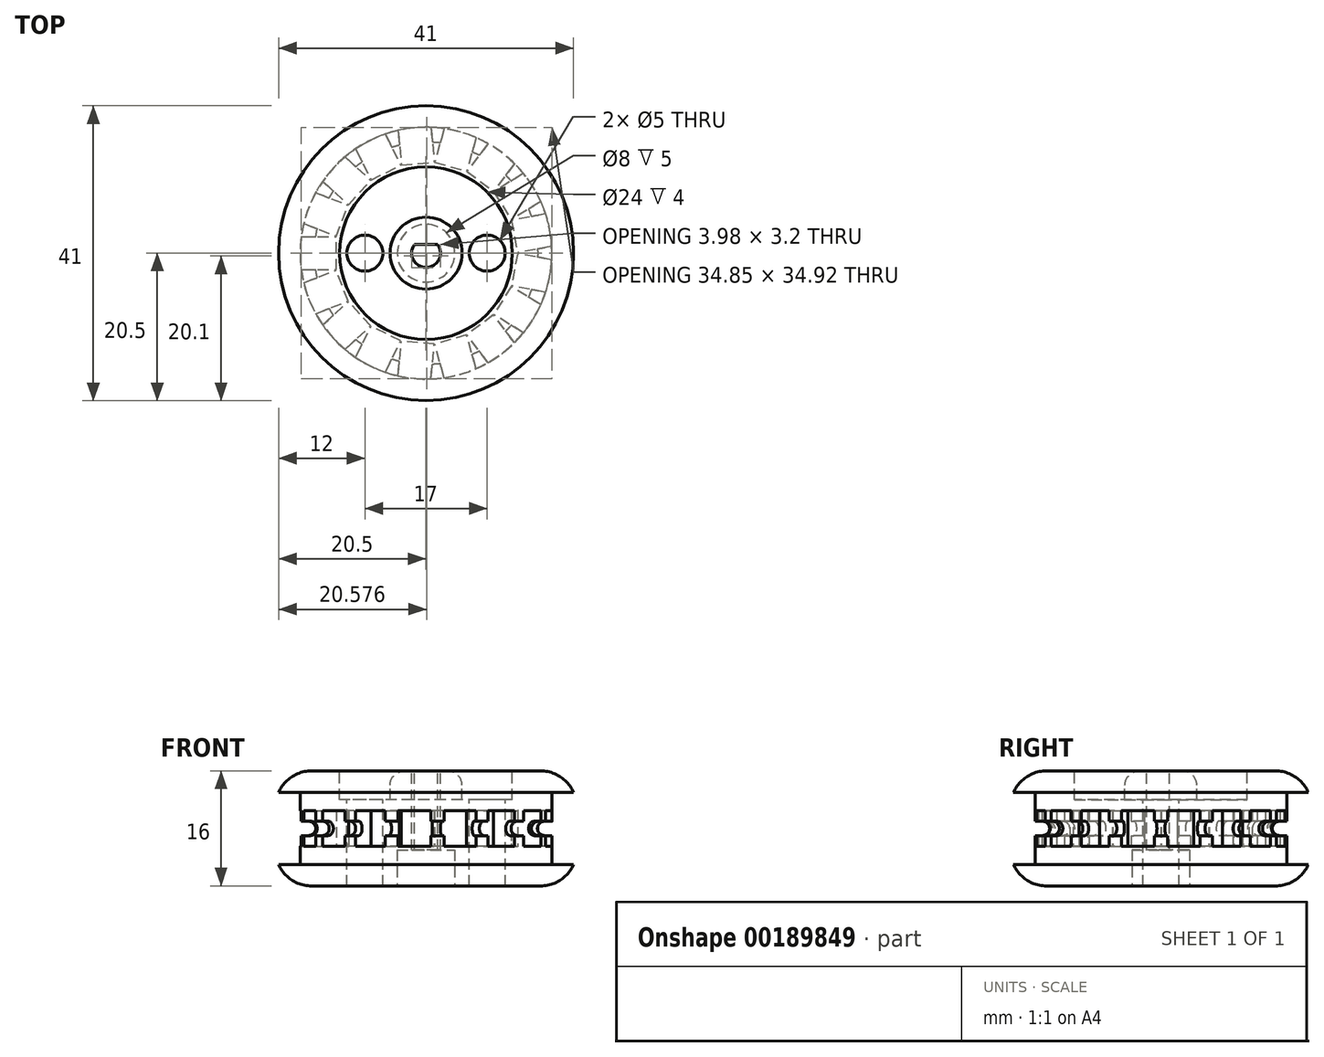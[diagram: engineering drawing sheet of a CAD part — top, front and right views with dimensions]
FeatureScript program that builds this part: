
annotation { "Feature Type Name" : "Feature", "Feature Type Description" : "" }
export const myFeature = defineFeature(function(context is Context, id is Id, definition is map)
    precondition{}
    {
        {
            var Q0;
            Q0=qCreatedBy(makeId("Top.planeOp"),FACE);
            var sketch = newSketch(context, id + "F0", { "sketchPlane" : qUnion([Q0])});
            skCircle(sketch, "E0", {"center": v(0, 0) * mm, "radius": 17.5 * mm});
            skSolve(sketch);
        }
        {
            var Q0;
            Q0=makeQuery(id+"F0.imprint","IMPRINT",FACE,{"disambiguationData":[TD([[makeQuery(id+"F0.imprint","IMPRINT",EDGE,{"derivedFrom":sQuery(id+"F0.wireOp",EDGE,"E0")}),1.0]])]});
            extrude(context, id + "F1", {"entities" : qUnion([Q0]), "depth" : 10 * mm});
        }
        {
            var Q0;
            Q0=makeQuery(id+"F1.opExtrude","CAP_FACE",FACE,{"disambiguationData":[OSD([sQuery(id+"F0.wireOp",EDGE,"E0")])],"isStart":false});
            cPlane(context, id + "F2", {"entities" : qUnion([Q0]), "cplaneType" : CPlaneType.OFFSET, "offset" : 5 * mm, "oppositeDirection" : true, "width" : 150 * mm, "height" : 150 * mm});
        }
        {
            var Q0;
            Q0=qCreatedBy(id+"F2.planeOp",FACE);
            var sketch = newSketch(context, id + "F3", { "sketchPlane" : qUnion([Q0])});
            skLineSegment(sketch, "E1.bottom", {"start": v(-17.5, -2.3) * mm, "end": v(-12.5, -2.3) * mm});
            skLineSegment(sketch, "E1.top", {"start": v(-17.5, 2.3) * mm, "end": v(-12.5, 2.3) * mm});
            skLineSegment(sketch, "E1.left", {"start": v(-17.5, -2.3) * mm, "end": v(-17.5, 2.3) * mm});
            skLineSegment(sketch, "E1.right", {"start": v(-12.5, -2.3) * mm, "end": v(-12.5, 2.3) * mm});
            skPoint(sketch, "E2", {"position": v(-12.5, 0) * mm});
            skLineSegment(sketch, "E3.1.0", {"start": v(-15.49, -8.47) * mm, "end": v(-10.83, -6.66) * mm});
            skLineSegment(sketch, "E3.1.1", {"start": v(-15.49, -8.47) * mm, "end": v(-17.15, -4.18) * mm});
            skLineSegment(sketch, "E3.1.2", {"start": v(-10.83, -6.66) * mm, "end": v(-12.49, -2.37) * mm});
            skLineSegment(sketch, "E3.1.3", {"start": v(-17.15, -4.18) * mm, "end": v(-12.49, -2.37) * mm});
            skLineSegment(sketch, "E3.2.0", {"start": v(-11.38, -13.49) * mm, "end": v(-7.69, -10.12) * mm});
            skLineSegment(sketch, "E3.2.1", {"start": v(-11.38, -13.49) * mm, "end": v(-14.48, -10.09) * mm});
            skLineSegment(sketch, "E3.2.2", {"start": v(-7.69, -10.12) * mm, "end": v(-10.79, -6.72) * mm});
            skLineSegment(sketch, "E3.2.3", {"start": v(-14.48, -10.09) * mm, "end": v(-10.79, -6.72) * mm});
            skLineSegment(sketch, "E3.3.0", {"start": v(-5.74, -16.7) * mm, "end": v(-3.51, -12.21) * mm});
            skLineSegment(sketch, "E3.3.1", {"start": v(-5.74, -16.7) * mm, "end": v(-9.86, -14.64) * mm});
            skLineSegment(sketch, "E3.3.2", {"start": v(-3.51, -12.21) * mm, "end": v(-7.63, -10.16) * mm});
            skLineSegment(sketch, "E3.3.3", {"start": v(-9.86, -14.64) * mm, "end": v(-7.63, -10.16) * mm});
            skLineSegment(sketch, "E3.4.0", {"start": v(0.68, -17.64) * mm, "end": v(1.14, -12.66) * mm});
            skLineSegment(sketch, "E3.4.1", {"start": v(0.68, -17.64) * mm, "end": v(-3.9, -17.21) * mm});
            skLineSegment(sketch, "E3.4.2", {"start": v(1.14, -12.66) * mm, "end": v(-3.44, -12.23) * mm});
            skLineSegment(sketch, "E3.4.3", {"start": v(-3.9, -17.21) * mm, "end": v(-3.44, -12.23) * mm});
            skLineSegment(sketch, "E3.5.0", {"start": v(7, -16.2) * mm, "end": v(5.63, -11.4) * mm});
            skLineSegment(sketch, "E3.5.1", {"start": v(7, -16.2) * mm, "end": v(2.58, -17.46) * mm});
            skLineSegment(sketch, "E3.5.2", {"start": v(5.63, -11.4) * mm, "end": v(1.2, -12.65) * mm});
            skLineSegment(sketch, "E3.5.3", {"start": v(2.58, -17.46) * mm, "end": v(1.2, -12.65) * mm});
            skLineSegment(sketch, "E3.6.0", {"start": v(12.38, -12.58) * mm, "end": v(9.37, -8.59) * mm});
            skLineSegment(sketch, "E3.6.1", {"start": v(12.38, -12.58) * mm, "end": v(8.71, -15.35) * mm});
            skLineSegment(sketch, "E3.6.2", {"start": v(9.37, -8.59) * mm, "end": v(5.7, -11.36) * mm});
            skLineSegment(sketch, "E3.6.3", {"start": v(8.71, -15.35) * mm, "end": v(5.7, -11.36) * mm});
            skLineSegment(sketch, "E3.7.0", {"start": v(16.09, -7.26) * mm, "end": v(11.84, -4.62) * mm});
            skLineSegment(sketch, "E3.7.1", {"start": v(16.09, -7.26) * mm, "end": v(13.67, -11.17) * mm});
            skLineSegment(sketch, "E3.7.2", {"start": v(11.84, -4.62) * mm, "end": v(9.42, -8.54) * mm});
            skLineSegment(sketch, "E3.7.3", {"start": v(13.67, -11.17) * mm, "end": v(9.42, -8.54) * mm});
            skLineSegment(sketch, "E3.8.0", {"start": v(17.62, -0.95) * mm, "end": v(12.7, -0.04) * mm});
            skLineSegment(sketch, "E3.8.1", {"start": v(17.62, -0.95) * mm, "end": v(16.78, -5.48) * mm});
            skLineSegment(sketch, "E3.8.2", {"start": v(12.7, -0.04) * mm, "end": v(11.86, -4.56) * mm});
            skLineSegment(sketch, "E3.8.3", {"start": v(16.78, -5.48) * mm, "end": v(11.86, -4.56) * mm});
            skLineSegment(sketch, "E3.9.0", {"start": v(16.78, 5.48) * mm, "end": v(11.86, 4.56) * mm});
            skLineSegment(sketch, "E3.9.1", {"start": v(16.78, 5.48) * mm, "end": v(17.62, 0.95) * mm});
            skLineSegment(sketch, "E3.9.2", {"start": v(11.86, 4.56) * mm, "end": v(12.7, 0.04) * mm});
            skLineSegment(sketch, "E3.9.3", {"start": v(17.62, 0.95) * mm, "end": v(12.7, 0.04) * mm});
            skLineSegment(sketch, "E3.10.0", {"start": v(13.67, 11.17) * mm, "end": v(9.42, 8.54) * mm});
            skLineSegment(sketch, "E3.10.1", {"start": v(13.67, 11.17) * mm, "end": v(16.09, 7.26) * mm});
            skLineSegment(sketch, "E3.10.2", {"start": v(9.42, 8.54) * mm, "end": v(11.84, 4.62) * mm});
            skLineSegment(sketch, "E3.10.3", {"start": v(16.09, 7.26) * mm, "end": v(11.84, 4.62) * mm});
            skLineSegment(sketch, "E3.11.0", {"start": v(8.71, 15.35) * mm, "end": v(5.7, 11.36) * mm});
            skLineSegment(sketch, "E3.11.1", {"start": v(8.71, 15.35) * mm, "end": v(12.38, 12.58) * mm});
            skLineSegment(sketch, "E3.11.2", {"start": v(5.7, 11.36) * mm, "end": v(9.37, 8.59) * mm});
            skLineSegment(sketch, "E3.11.3", {"start": v(12.38, 12.58) * mm, "end": v(9.37, 8.59) * mm});
            skLineSegment(sketch, "E3.12.0", {"start": v(2.58, 17.46) * mm, "end": v(1.2, 12.65) * mm});
            skLineSegment(sketch, "E3.12.1", {"start": v(2.58, 17.46) * mm, "end": v(7, 16.2) * mm});
            skLineSegment(sketch, "E3.12.2", {"start": v(1.2, 12.65) * mm, "end": v(5.63, 11.4) * mm});
            skLineSegment(sketch, "E3.12.3", {"start": v(7, 16.2) * mm, "end": v(5.63, 11.4) * mm});
            skLineSegment(sketch, "E3.13.0", {"start": v(-3.9, 17.21) * mm, "end": v(-3.44, 12.23) * mm});
            skLineSegment(sketch, "E3.13.1", {"start": v(-3.9, 17.21) * mm, "end": v(0.68, 17.64) * mm});
            skLineSegment(sketch, "E3.13.2", {"start": v(-3.44, 12.23) * mm, "end": v(1.14, 12.66) * mm});
            skLineSegment(sketch, "E3.13.3", {"start": v(0.68, 17.64) * mm, "end": v(1.14, 12.66) * mm});
            skLineSegment(sketch, "E3.14.0", {"start": v(-9.86, 14.64) * mm, "end": v(-7.63, 10.16) * mm});
            skLineSegment(sketch, "E3.14.1", {"start": v(-9.86, 14.64) * mm, "end": v(-5.74, 16.7) * mm});
            skLineSegment(sketch, "E3.14.2", {"start": v(-7.63, 10.16) * mm, "end": v(-3.51, 12.21) * mm});
            skLineSegment(sketch, "E3.14.3", {"start": v(-5.74, 16.7) * mm, "end": v(-3.51, 12.21) * mm});
            skLineSegment(sketch, "E3.15.0", {"start": v(-14.48, 10.09) * mm, "end": v(-10.79, 6.72) * mm});
            skLineSegment(sketch, "E3.15.1", {"start": v(-14.48, 10.09) * mm, "end": v(-11.38, 13.49) * mm});
            skLineSegment(sketch, "E3.15.2", {"start": v(-10.79, 6.72) * mm, "end": v(-7.69, 10.12) * mm});
            skLineSegment(sketch, "E3.15.3", {"start": v(-11.38, 13.49) * mm, "end": v(-7.69, 10.12) * mm});
            skLineSegment(sketch, "E3.16.0", {"start": v(-17.15, 4.18) * mm, "end": v(-12.49, 2.37) * mm});
            skLineSegment(sketch, "E3.16.1", {"start": v(-17.15, 4.18) * mm, "end": v(-15.49, 8.47) * mm});
            skLineSegment(sketch, "E3.16.2", {"start": v(-12.49, 2.37) * mm, "end": v(-10.83, 6.66) * mm});
            skLineSegment(sketch, "E3.16.3", {"start": v(-15.49, 8.47) * mm, "end": v(-10.83, 6.66) * mm});
            skPoint(sketch, "E3.center", {"position": v(0, 0) * mm});
            skSolve(sketch);
        }
        {
            var Q0;
            Q0=makeQuery(id+"F1.opExtrude","CAP_FACE",FACE,{"disambiguationData":[OSD([sQuery(id+"F0.wireOp",EDGE,"E0")])],"isStart":false});
            var sketch = newSketch(context, id + "F4", { "sketchPlane" : qUnion([Q0])});
            skPoint(sketch, "E4", {"position": v(-17.5, 0) * mm});
            skSolve(sketch);
        }
        {
            var Q0;
            Q0=qCreatedBy(makeId("Front.planeOp"),FACE);
            var sketch = newSketch(context, id + "F5", { "sketchPlane" : qUnion([Q0])});
            skArc(sketch, "E5", {"start": v(-16.5, 4) * mm, "mid": v(-15.5, 5) * mm, "end": v(-16.5, 6) * mm});
            skLineSegment(sketch, "E6.bottom", {"start": v(-16.5, 6) * mm, "end": v(-17.5, 6) * mm});
            skLineSegment(sketch, "E6.top", {"start": v(-16.5, 4) * mm, "end": v(-17.5, 4) * mm});
            skLineSegment(sketch, "E6.right", {"start": v(-17.5, 6) * mm, "end": v(-17.5, 4) * mm});
            skLineSegment(sketch, "E7", {"start": v(-17.5, 10) * mm, "end": v(-17.5, 0) * mm});
            skPoint(sketch, "E8", {"position": v(-17.5, 5) * mm});
            skLineSegment(sketch, "E9", {"start": v(0, 0) * mm, "end": v(0, 9.87) * mm});
            skSolve(sketch);
        }
        {
            var Q0;
            Q0=makeQuery(id+"F1.opExtrude","CAP_FACE",FACE,{"disambiguationData":[OSD([sQuery(id+"F0.wireOp",EDGE,"E0")])],"isStart":false});
            var sketch = newSketch(context, id + "F6", { "sketchPlane" : qUnion([Q0])});
            skPoint(sketch, "E10", {"position": v(-17.5, 0) * mm});
            skSolve(sketch);
        }
        {
            var Q0;
            Q0=makeQuery(id+"F1.opExtrude","CAP_FACE",FACE,{"disambiguationData":[OSD([sQuery(id+"F0.wireOp",EDGE,"E0")])],"isStart":true});
            var sketch = newSketch(context, id + "F7", { "sketchPlane" : qUnion([Q0])});
            skPoint(sketch, "E11", {"position": v(-17.5, 0) * mm});
            skSolve(sketch);
        }
        {
            var Q0;
            Q0=makeQuery(id+"F6.imprint","IMPRINT",FACE,{"disambiguationData":[TD([[makeQuery(id+"F6.imprint","IMPRINT",EDGE,{"derivedFrom":makeQuery(id+"F1.opExtrude","CAP_EDGE",EDGE,{"disambiguationData":[OSD([sQuery(id+"F0.wireOp",EDGE,"E0")])],"isStart":false})}),1.0]])]});
            var sketch = newSketch(context, id + "F8", { "sketchPlane" : qUnion([Q0])});
            skCircle(sketch, "E12", {"center": v(0, 0) * mm, "radius": 20.5 * mm});
            skSolve(sketch);
        }
        {
            var Q0;
            Q0=makeQuery(id+"F8.imprint","IMPRINT",FACE,{"disambiguationData":[TD([[makeQuery(id+"F8.imprint","IMPRINT",EDGE,{"derivedFrom":sQuery(id+"F8.wireOp",EDGE,"E12")}),1.0]])]});
            var Q1;
            Q1=makeQuery(id+"F6.imprint","IMPRINT",FACE,{"disambiguationData":[TD([[makeQuery(id+"F6.imprint","IMPRINT",EDGE,{"derivedFrom":makeQuery(id+"F1.opExtrude","CAP_EDGE",EDGE,{"disambiguationData":[OSD([sQuery(id+"F0.wireOp",EDGE,"E0")])],"isStart":false})}),1.0]])]});
            extrude(context, id + "F9", {"entities" : qUnion([Q0, Q1]), "operationType" : NewBodyOperationType.ADD, "depth" : 3 * mm});
        }
        {
            var Q0;
            Q0=makeQuery(id+"F7.imprint","IMPRINT",FACE,{"disambiguationData":[TD([[makeQuery(id+"F7.imprint","IMPRINT",EDGE,{"derivedFrom":makeQuery(id+"F1.opExtrude","CAP_EDGE",EDGE,{"disambiguationData":[OSD([sQuery(id+"F0.wireOp",EDGE,"E0")])],"isStart":true})}),-1.0]])]});
            var sketch = newSketch(context, id + "F10", { "sketchPlane" : qUnion([Q0])});
            skCircle(sketch, "E13", {"center": v(0, 0) * mm, "radius": 20.5 * mm});
            skSolve(sketch);
        }
        {
            var Q0;
            Q0=makeQuery(id+"F7.imprint","IMPRINT",FACE,{"disambiguationData":[TD([[makeQuery(id+"F7.imprint","IMPRINT",EDGE,{"derivedFrom":makeQuery(id+"F1.opExtrude","CAP_EDGE",EDGE,{"disambiguationData":[OSD([sQuery(id+"F0.wireOp",EDGE,"E0")])],"isStart":true})}),-1.0]])]});
            var Q1;
            Q1=makeQuery(id+"F10.imprint","IMPRINT",FACE,{"disambiguationData":[TD([[makeQuery(id+"F10.imprint","IMPRINT",EDGE,{"derivedFrom":sQuery(id+"F10.wireOp",EDGE,"E13")}),1.0]])]});
            extrude(context, id + "F11", {"entities" : qUnion([Q0, Q1]), "operationType" : NewBodyOperationType.ADD, "depth" : 3 * mm});
        }
        {
            var Q0;
            Q0=makeQuery(id+"F11.opExtrude","CAP_EDGE",EDGE,{"disambiguationData":[OSD([sQuery(id+"F10.wireOp",EDGE,"E13")])],"isStart":false});
            var Q1;
            Q1=makeQuery(id+"F9.opExtrude","CAP_EDGE",EDGE,{"disambiguationData":[OSD([sQuery(id+"F8.wireOp",EDGE,"E12")])],"isStart":false});
            fillet(context, id + "F12", {"entities" : qUnion([Q0, Q1]), "radius" : 5 * mm, "tangentPropagation" : true, "allowEdgeOverflow" : false});
        }
        {
            var Q0;
            {var subQ0=sQuery(id+"F0.wireOp",EDGE,"E0");Q0=makeQuery(id+"F9.boolean.opBoolean","MERGE",FACE,{"derivedFrom":[makeQuery(id+"F9.opExtrude","CAP_FACE",FACE,{"disambiguationData":[OSD([subQ0])],"isStart":false}),makeQuery(id+"F9.opExtrude","CAP_FACE",FACE,{"disambiguationData":[OSD([subQ0,sQuery(id+"F8.wireOp",EDGE,"E12")])],"isStart":false})]});}
            var sketch = newSketch(context, id + "F13", { "sketchPlane" : qUnion([Q0])});
            skCircle(sketch, "E14", {"center": v(0, 0) * mm, "radius": 2 * mm});
            skLineSegment(sketch, "E15", {"start": v(-1.6, 1.2) * mm, "end": v(1.6, 1.2) * mm});
            skSolve(sketch);
        }
        {
            var Q0;
            {var subQ0=sQuery(id+"F13.wireOp",EDGE,"E15");Q0=makeQuery(id+"F13.imprint","IMPRINT",FACE,{"disambiguationData":[TD([[makeQuery(id+"F13.imprint","IMPRINT",EDGE,{"derivedFrom":subQ0}),-1.0]])]});}
            extrude(context, id + "F14", {"entities" : qUnion([Q0]), "operationType" : NewBodyOperationType.REMOVE, "endBound" : BoundingType.THROUGH_ALL, "oppositeDirection" : true, "depth" : 25 * mm});
        }
        {
            var Q0;
            {var subQ0=sQuery(id+"F0.wireOp",EDGE,"E0");Q0=makeQuery(id+"F11.boolean.opBoolean","MERGE",FACE,{"derivedFrom":[makeQuery(id+"F11.opExtrude","CAP_FACE",FACE,{"disambiguationData":[OSD([subQ0])],"isStart":false}),makeQuery(id+"F11.opExtrude","CAP_FACE",FACE,{"disambiguationData":[OSD([subQ0,sQuery(id+"F10.wireOp",EDGE,"E13")])],"isStart":false})]});}
            var sketch = newSketch(context, id + "F15", { "sketchPlane" : qUnion([Q0])});
            skCircle(sketch, "E16", {"center": v(0, 0) * mm, "radius": 4 * mm});
            skSolve(sketch);
        }
        {
            var Q0;
            Q0=makeQuery(id+"F15.imprint","IMPRINT",FACE,{"disambiguationData":[TD([[makeQuery(id+"F15.imprint","IMPRINT",EDGE,{"derivedFrom":sQuery(id+"F15.wireOp",EDGE,"E16")}),1.0]])]});
            extrude(context, id + "F16", {"entities" : qUnion([Q0]), "operationType" : NewBodyOperationType.REMOVE, "oppositeDirection" : true, "depth" : 5 * mm});
        }
        {
            var Q0;
            {var subQ0=sQuery(id+"F0.wireOp",EDGE,"E0");Q0=makeQuery(id+"F9.boolean.opBoolean","MERGE",FACE,{"derivedFrom":[makeQuery(id+"F9.opExtrude","CAP_FACE",FACE,{"disambiguationData":[OSD([subQ0])],"isStart":false}),makeQuery(id+"F9.opExtrude","CAP_FACE",FACE,{"disambiguationData":[OSD([subQ0,sQuery(id+"F8.wireOp",EDGE,"E12")])],"isStart":false})]});}
            var sketch = newSketch(context, id + "F17", { "sketchPlane" : qUnion([Q0])});
            skCircle(sketch, "E17", {"center": v(0, 0) * mm, "radius": 8.5 * mm});
            skCircle(sketch, "E18", {"center": v(0, 0) * mm, "radius": 12 * mm});
            skCircle(sketch, "E19", {"center": v(0, 0) * mm, "radius": 5 * mm});
            skSolve(sketch);
        }
        {
            var Q0;
            Q0=makeQuery(id+"F17.imprint","IMPRINT",FACE,{"disambiguationData":[TD([[makeQuery(id+"F17.imprint","IMPRINT",EDGE,{"derivedFrom":sQuery(id+"F17.wireOp",EDGE,"E17")}),-1.0]])]});
            var Q1;
            Q1=makeQuery(id+"F17.imprint","IMPRINT",FACE,{"disambiguationData":[TD([[makeQuery(id+"F17.imprint","IMPRINT",EDGE,{"derivedFrom":sQuery(id+"F17.wireOp",EDGE,"E17")}),1.0]])]});
            extrude(context, id + "F18", {"entities" : qUnion([Q0, Q1]), "operationType" : NewBodyOperationType.REMOVE, "oppositeDirection" : true, "depth" : 4 * mm});
        }
        {
            var Q0;
            Q0=makeQuery(id+"F18.boolean.opBoolean","COPY",EDGE,{"derivedFrom":makeQuery(id+"F18.opExtrude","CAP_EDGE",EDGE,{"disambiguationData":[OSD([sQuery(id+"F17.wireOp",EDGE,"E18")])],"isStart":true})});
            var Q1;
            Q1=makeQuery(id+"F18.boolean.opBoolean","COPY",EDGE,{"derivedFrom":makeQuery(id+"F18.opExtrude","CAP_EDGE",EDGE,{"disambiguationData":[OSD([sQuery(id+"F17.wireOp",EDGE,"E19")])],"isStart":true})});
            fillet(context, id + "F19", {"entities" : qUnion([Q0, Q1]), "radius" : 2 * mm, "tangentPropagation" : true, "allowEdgeOverflow" : false});
        }
        {
            var Q0;
            Q0=makeQuery(id+"F3.imprint","IMPRINT",FACE,{"disambiguationData":[TD([[makeQuery(id+"F3.imprint","IMPRINT",EDGE,{"derivedFrom":sQuery(id+"F3.wireOp",EDGE,"E3.2.0")}),1.0]])]});
            var Q1;
            Q1=makeQuery(id+"F3.imprint","IMPRINT",FACE,{"disambiguationData":[TD([[makeQuery(id+"F3.imprint","IMPRINT",EDGE,{"derivedFrom":sQuery(id+"F3.wireOp",EDGE,"E3.1.0")}),1.0]])]});
            var Q2;
            Q2=makeQuery(id+"F3.imprint","IMPRINT",FACE,{"disambiguationData":[TD([[makeQuery(id+"F3.imprint","IMPRINT",EDGE,{"derivedFrom":sQuery(id+"F3.wireOp",EDGE,"E1.bottom")}),1.0]])]});
            var Q3;
            Q3=makeQuery(id+"F3.imprint","IMPRINT",FACE,{"disambiguationData":[TD([[makeQuery(id+"F3.imprint","IMPRINT",EDGE,{"derivedFrom":sQuery(id+"F3.wireOp",EDGE,"E3.16.0")}),1.0]])]});
            var Q4;
            Q4=makeQuery(id+"F3.imprint","IMPRINT",FACE,{"disambiguationData":[TD([[makeQuery(id+"F3.imprint","IMPRINT",EDGE,{"derivedFrom":sQuery(id+"F3.wireOp",EDGE,"E3.15.0")}),1.0]])]});
            var Q5;
            Q5=makeQuery(id+"F3.imprint","IMPRINT",FACE,{"disambiguationData":[TD([[makeQuery(id+"F3.imprint","IMPRINT",EDGE,{"derivedFrom":sQuery(id+"F3.wireOp",EDGE,"E3.14.0")}),1.0]])]});
            var Q6;
            Q6=makeQuery(id+"F3.imprint","IMPRINT",FACE,{"disambiguationData":[TD([[makeQuery(id+"F3.imprint","IMPRINT",EDGE,{"derivedFrom":sQuery(id+"F3.wireOp",EDGE,"E3.13.0")}),1.0]])]});
            var Q7;
            Q7=makeQuery(id+"F3.imprint","IMPRINT",FACE,{"disambiguationData":[TD([[makeQuery(id+"F3.imprint","IMPRINT",EDGE,{"derivedFrom":sQuery(id+"F3.wireOp",EDGE,"E3.12.0")}),1.0]])]});
            var Q8;
            Q8=makeQuery(id+"F3.imprint","IMPRINT",FACE,{"disambiguationData":[TD([[makeQuery(id+"F3.imprint","IMPRINT",EDGE,{"derivedFrom":sQuery(id+"F3.wireOp",EDGE,"E3.11.0")}),1.0]])]});
            var Q9;
            Q9=makeQuery(id+"F3.imprint","IMPRINT",FACE,{"disambiguationData":[TD([[makeQuery(id+"F3.imprint","IMPRINT",EDGE,{"derivedFrom":sQuery(id+"F3.wireOp",EDGE,"E3.10.0")}),1.0]])]});
            var Q10;
            Q10=makeQuery(id+"F3.imprint","IMPRINT",FACE,{"disambiguationData":[TD([[makeQuery(id+"F3.imprint","IMPRINT",EDGE,{"derivedFrom":sQuery(id+"F3.wireOp",EDGE,"E3.9.0")}),1.0]])]});
            var Q11;
            Q11=makeQuery(id+"F3.imprint","IMPRINT",FACE,{"disambiguationData":[TD([[makeQuery(id+"F3.imprint","IMPRINT",EDGE,{"derivedFrom":sQuery(id+"F3.wireOp",EDGE,"E3.8.0")}),1.0]])]});
            var Q12;
            Q12=makeQuery(id+"F3.imprint","IMPRINT",FACE,{"disambiguationData":[TD([[makeQuery(id+"F3.imprint","IMPRINT",EDGE,{"derivedFrom":sQuery(id+"F3.wireOp",EDGE,"E3.7.0")}),1.0]])]});
            var Q13;
            Q13=makeQuery(id+"F3.imprint","IMPRINT",FACE,{"disambiguationData":[TD([[makeQuery(id+"F3.imprint","IMPRINT",EDGE,{"derivedFrom":sQuery(id+"F3.wireOp",EDGE,"E3.6.0")}),1.0]])]});
            var Q14;
            Q14=makeQuery(id+"F3.imprint","IMPRINT",FACE,{"disambiguationData":[TD([[makeQuery(id+"F3.imprint","IMPRINT",EDGE,{"derivedFrom":sQuery(id+"F3.wireOp",EDGE,"E3.5.0")}),1.0]])]});
            var Q15;
            Q15=makeQuery(id+"F3.imprint","IMPRINT",FACE,{"disambiguationData":[TD([[makeQuery(id+"F3.imprint","IMPRINT",EDGE,{"derivedFrom":sQuery(id+"F3.wireOp",EDGE,"E3.4.0")}),1.0]])]});
            var Q16;
            Q16=makeQuery(id+"F3.imprint","IMPRINT",FACE,{"disambiguationData":[TD([[makeQuery(id+"F3.imprint","IMPRINT",EDGE,{"derivedFrom":sQuery(id+"F3.wireOp",EDGE,"E3.3.0")}),1.0]])]});
            extrude(context, id + "F20", {"entities" : qUnion([Q0, Q1, Q2, Q3, Q4, Q5, Q6, Q7, Q8, Q9, Q10, Q11, Q12, Q13, Q14, Q15, Q16]), "operationType" : NewBodyOperationType.REMOVE, "endBound" : BoundingType.SYMMETRIC, "depth" : 5 * mm});
        }
        {
            var Q0;
            Q0=makeQuery(id+"F5.imprint","IMPRINT",FACE,{"disambiguationData":[TD([[makeQuery(id+"F5.imprint","IMPRINT",EDGE,{"derivedFrom":sQuery(id+"F5.wireOp",EDGE,"E5")}),1.0]])]});
            var Q1;
            Q1=sQuery(id+"F5.wireOp",EDGE,"E9");
            revolve(context, id + "F21", {"operationType" : NewBodyOperationType.REMOVE, "entities" : qUnion([Q0]), "axis" : qUnion([Q1]), "revolveType" : RevolveType.FULL, "oppositeDirection" : true});
        }
        {
            var Q0;
            Q0=makeQuery(id+"F4.imprint","IMPRINT",FACE,{"disambiguationData":[TD([[makeQuery(id+"F4.imprint","IMPRINT",EDGE,{"derivedFrom":makeQuery(id+"F1.opExtrude","CAP_EDGE",EDGE,{"disambiguationData":[OSD([sQuery(id+"F0.wireOp",EDGE,"E0")])],"isStart":false})}),1.0]])]});
            var sketch = newSketch(context, id + "F22", { "sketchPlane" : qUnion([Q0])});
            skCircle(sketch, "E20", {"center": v(-8.5, 0) * mm, "radius": 2.5 * mm});
            skCircle(sketch, "E21", {"center": v(8.5, 0) * mm, "radius": 2.5 * mm});
            skSolve(sketch);
        }
        {
            var Q0;
            Q0=makeQuery(id+"F22.imprint","IMPRINT",FACE,{"disambiguationData":[TD([[makeQuery(id+"F22.imprint","IMPRINT",EDGE,{"derivedFrom":sQuery(id+"F22.wireOp",EDGE,"E20")}),1.0]])]});
            var Q1;
            Q1=makeQuery(id+"F22.imprint","IMPRINT",FACE,{"disambiguationData":[TD([[makeQuery(id+"F22.imprint","IMPRINT",EDGE,{"derivedFrom":sQuery(id+"F22.wireOp",EDGE,"E21")}),1.0]])]});
            var Q2;
            {var subQ0=sQuery(id+"F0.wireOp",EDGE,"E0");Q2=makeQuery(id+"F11.boolean.opBoolean","MERGE",FACE,{"derivedFrom":[makeQuery(id+"F11.opExtrude","CAP_FACE",FACE,{"disambiguationData":[OSD([subQ0])],"isStart":false}),makeQuery(id+"F11.opExtrude","CAP_FACE",FACE,{"disambiguationData":[OSD([subQ0,sQuery(id+"F10.wireOp",EDGE,"E13")])],"isStart":false})]});}
            extrude(context, id + "F23", {"entities" : qUnion([Q0, Q1]), "operationType" : NewBodyOperationType.REMOVE, "endBound" : BoundingType.UP_TO_SURFACE, "oppositeDirection" : true, "endBoundEntityFace" : qUnion([Q2]), "depth" : 25 * mm});
        }
    });
